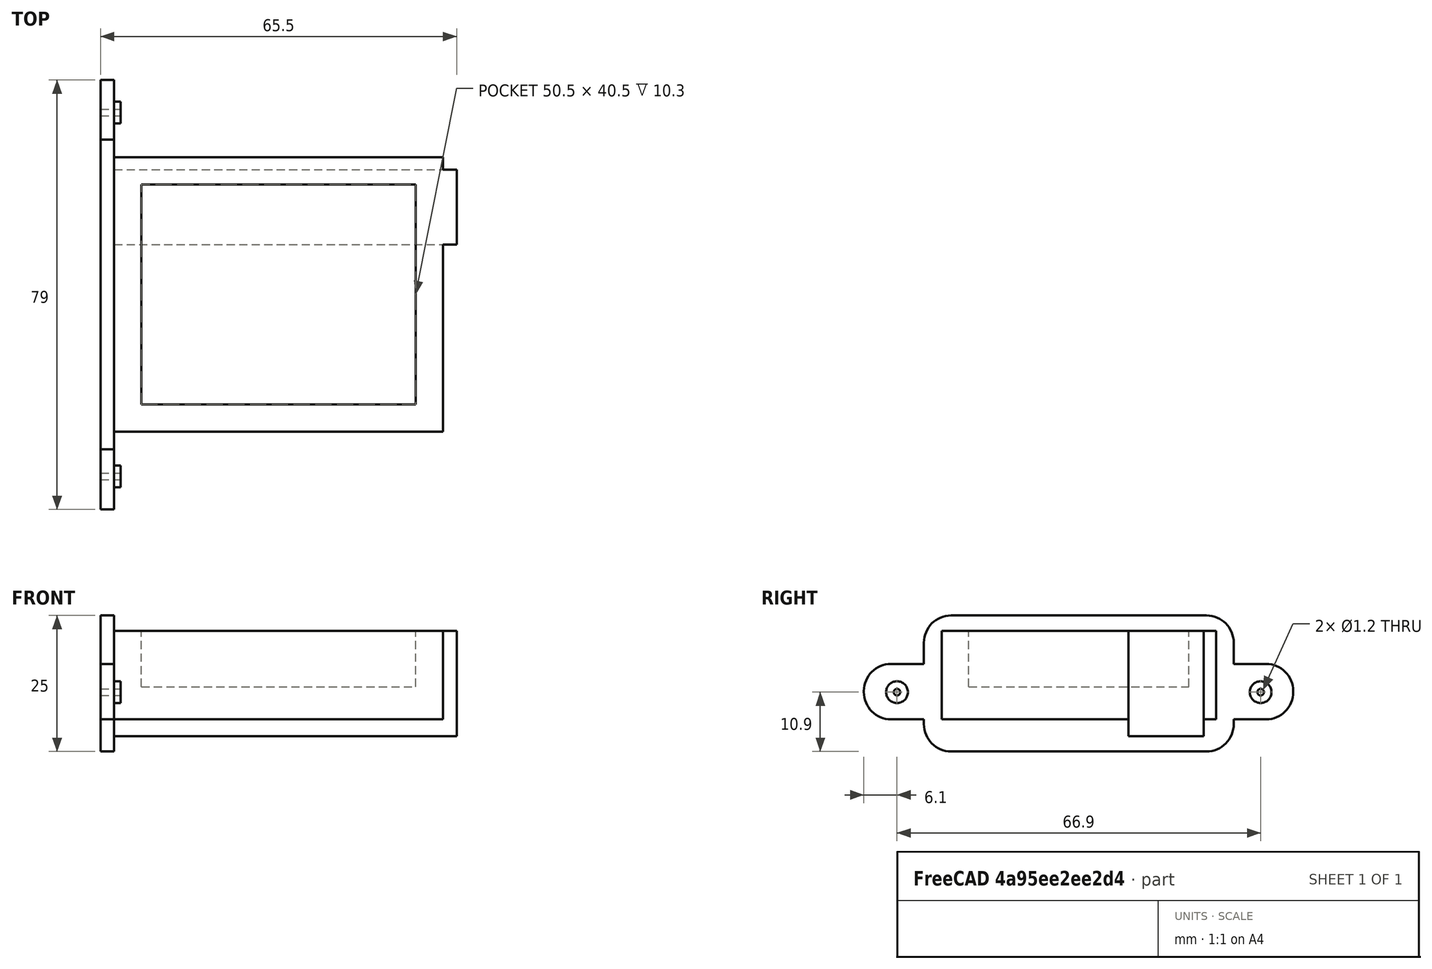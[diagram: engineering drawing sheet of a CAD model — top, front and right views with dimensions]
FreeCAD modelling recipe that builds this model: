
FCSTD DOCUMENT  (FreeCAD 0.18.4R)
Label: chicco-next2star-power-adapter
License: All rights reserved
LicenseURL: http://en.wikipedia.org/wiki/All_rights_reserved
objects: Part::Box×5, Part::Cylinder×4, Part::MultiFuse×3, Part::Cut×3, Part::Fillet×2
note: 17 computed .brp shape members not serialized (recipe doc carries the construction recipe); baked Part::Feature solids carry a one-line shape summary decoded from their .brp

FEATURE [Part::Box] Box  label="Cube"
  AttacherType = Attacher::AttachEngine3D
  Height = 16.3
  Length = 60.5
  Width = 50.5
FEATURE [Part::Box] Box001  label="Cube001"
  AttacherType = Attacher::AttachEngine3D
  Height = 19.4
  Length = 63
  Placement = pos=(0,34.4,-3.1) rot=(0,0,1;0rad)
  Width = 13.8
FEATURE [Part::Box] Box002  label="Cube002"
  AttacherType = Attacher::AttachEngine3D
  Height = 10.3
  Length = 50.5
  Placement = pos=(5,5,6) rot=(0,0,1;0rad)
  Width = 40.5
FEATURE [Part::MultiFuse] Fusion
  Shapes = -> [Box001,Box]
FEATURE [Part::Cut] Cut
  Base = -> Fusion
  Tool = -> Box002
FEATURE [Part::Box] Box003  label="Cube003"
  AttacherType = Attacher::AttachEngine3D
  Height = 25
  Length = 2.5
  Placement = pos=(-2.5,-3.25,-5.9) rot=(0,0,1;0rad)
  Width = 57
FEATURE [Part::Box] Box004  label="Cube004"
  AttacherType = Attacher::AttachEngine3D
  Height = 10.2
  Length = 2.5
  Placement = pos=(-2.5,-14.3,0) rot=(0,0,1;0rad)
  Width = 79
FEATURE [Part::Fillet] Fillet
  Base = -> Box003
  Edges = 4 edges r=5: [Edge9,Edge10,Edge11,Edge12]
FEATURE [Part::Fillet] Fillet001
  Base = -> Box004
  Edges = 4 edges r=5: [Edge9,Edge10,Edge11,Edge12]
FEATURE [Part::Cylinder] Cylinder
  Angle = 360
  AttacherType = Attacher::AttachEngine3D
  Height = 1.2
  Placement = pos=(0,-8.2,5) rot=(0,1,0;1.5708rad)
  Radius = 2
FEATURE [Part::Cylinder] Cylinder001  label="foro"
  Angle = 360
  AttacherType = Attacher::AttachEngine3D
  Height = 10
  Placement = pos=(-6,-8.2,5) rot=(0,1,0;1.5708rad)
  Radius = 0.6
FEATURE [Part::Cylinder] Cylinder002
  Angle = 360
  AttacherType = Attacher::AttachEngine3D
  Height = 1.2
  Placement = pos=(0,58.7,5) rot=(0,1,0;1.5708rad)
  Radius = 2
FEATURE [Part::Cylinder] Cylinder003  label="foro001"
  Angle = 360
  AttacherType = Attacher::AttachEngine3D
  Height = 10
  Placement = pos=(-6,58.7,5) rot=(0,1,0;1.5708rad)
  Radius = 0.6
FEATURE [Part::MultiFuse] Fusion001
  Shapes = -> [Fillet001,Cylinder,Cylinder002]
FEATURE [Part::Cut] Cut001
  Base = -> Fusion001
  Tool = -> Cylinder003
FEATURE [Part::Cut] Cut002
  Base = -> Cut001
  Tool = -> Cylinder001
FEATURE [Part::MultiFuse] Fusion002
  Shapes = -> [Cut002,Fillet,Cut]
